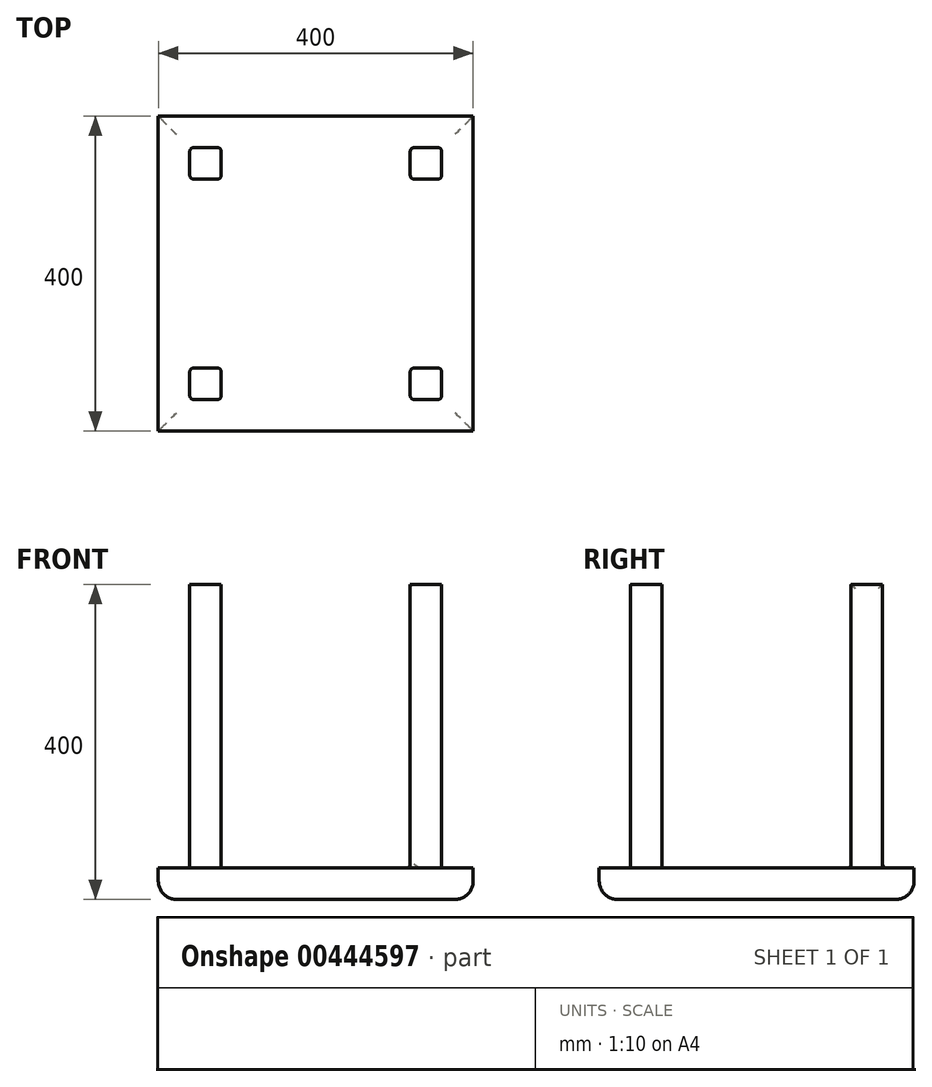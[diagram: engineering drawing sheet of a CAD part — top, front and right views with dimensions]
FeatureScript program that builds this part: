
annotation { "Feature Type Name" : "Feature", "Feature Type Description" : "" }
export const myFeature = defineFeature(function(context is Context, id is Id, definition is map)
    precondition{}
    {
        {
            var Q0;
            Q0=qCreatedBy(makeId("Top.planeOp"),FACE);
            var sketch = newSketch(context, id + "F0", { "sketchPlane" : qUnion([Q0])});
            skLineSegment(sketch, "E0.bottom", {"start": v(-209.5, 229.57) * mm, "end": v(190.5, 229.57) * mm});
            skLineSegment(sketch, "E0.top", {"start": v(-209.5, -170.43) * mm, "end": v(190.5, -170.43) * mm});
            skLineSegment(sketch, "E0.left", {"start": v(-209.5, 229.57) * mm, "end": v(-209.5, -170.43) * mm});
            skLineSegment(sketch, "E0.right", {"start": v(190.5, 229.57) * mm, "end": v(190.5, -170.43) * mm});
            skSolve(sketch);
        }
        {
            var Q0;
            Q0=makeQuery(id+"F0.imprint","IMPRINT",FACE,{"disambiguationData":[TD([[makeQuery(id+"F0.imprint","IMPRINT",EDGE,{"derivedFrom":sQuery(id+"F0.wireOp",EDGE,"E0.bottom")}),-1.0]])]});
            extrude(context, id + "F1", {"entities" : qUnion([Q0]), "depth" : 40 * mm});
        }
        {
            var Q0;
            Q0=makeQuery(id+"F1.opExtrude","CAP_FACE",FACE,{"disambiguationData":[OSD([sQuery(id+"F0.wireOp",EDGE,"E0.bottom"),sQuery(id+"F0.wireOp",EDGE,"E0.top"),sQuery(id+"F0.wireOp",EDGE,"E0.left"),sQuery(id+"F0.wireOp",EDGE,"E0.right")])],"isStart":false});
            var sketch = newSketch(context, id + "F2", { "sketchPlane" : qUnion([Q0])});
            skLineSegment(sketch, "E1.bottom", {"start": v(-169.5, 189.57) * mm, "end": v(-129.5, 189.57) * mm});
            skLineSegment(sketch, "E1.top", {"start": v(-169.5, 149.57) * mm, "end": v(-129.5, 149.57) * mm});
            skLineSegment(sketch, "E1.left", {"start": v(-169.5, 189.57) * mm, "end": v(-169.5, 149.57) * mm});
            skLineSegment(sketch, "E1.right", {"start": v(-129.5, 189.57) * mm, "end": v(-129.5, 149.57) * mm});
            skLineSegment(sketch, "E2.bottom", {"start": v(-169.5, -90.43) * mm, "end": v(-129.5, -90.43) * mm});
            skLineSegment(sketch, "E2.top", {"start": v(-169.5, -130.43) * mm, "end": v(-129.5, -130.43) * mm});
            skLineSegment(sketch, "E2.left", {"start": v(-169.5, -90.43) * mm, "end": v(-169.5, -130.43) * mm});
            skLineSegment(sketch, "E2.right", {"start": v(-129.5, -90.43) * mm, "end": v(-129.5, -130.43) * mm});
            skLineSegment(sketch, "E3.bottom", {"start": v(110.5, -90.43) * mm, "end": v(150.5, -90.43) * mm});
            skLineSegment(sketch, "E3.top", {"start": v(110.5, -130.43) * mm, "end": v(150.5, -130.43) * mm});
            skLineSegment(sketch, "E3.left", {"start": v(110.5, -90.43) * mm, "end": v(110.5, -130.43) * mm});
            skLineSegment(sketch, "E3.right", {"start": v(150.5, -90.43) * mm, "end": v(150.5, -130.43) * mm});
            skLineSegment(sketch, "E4.bottom", {"start": v(110.5, 189.57) * mm, "end": v(150.5, 189.57) * mm});
            skLineSegment(sketch, "E4.top", {"start": v(110.5, 149.57) * mm, "end": v(150.5, 149.57) * mm});
            skLineSegment(sketch, "E4.left", {"start": v(110.5, 189.57) * mm, "end": v(110.5, 149.57) * mm});
            skLineSegment(sketch, "E4.right", {"start": v(150.5, 189.57) * mm, "end": v(150.5, 149.57) * mm});
            skSolve(sketch);
        }
        {
            var Q0;
            Q0=makeQuery(id+"F2.imprint","IMPRINT",FACE,{"disambiguationData":[TD([[makeQuery(id+"F2.imprint","IMPRINT",EDGE,{"derivedFrom":sQuery(id+"F2.wireOp",EDGE,"E3.bottom")}),-1.0]])]});
            var Q1;
            Q1=makeQuery(id+"F2.imprint","IMPRINT",FACE,{"disambiguationData":[TD([[makeQuery(id+"F2.imprint","IMPRINT",EDGE,{"derivedFrom":sQuery(id+"F2.wireOp",EDGE,"E2.bottom")}),-1.0]])]});
            var Q2;
            Q2=makeQuery(id+"F2.imprint","IMPRINT",FACE,{"disambiguationData":[TD([[makeQuery(id+"F2.imprint","IMPRINT",EDGE,{"derivedFrom":sQuery(id+"F2.wireOp",EDGE,"E1.bottom")}),-1.0]])]});
            var Q3;
            Q3=makeQuery(id+"F2.imprint","IMPRINT",FACE,{"disambiguationData":[TD([[makeQuery(id+"F2.imprint","IMPRINT",EDGE,{"derivedFrom":sQuery(id+"F2.wireOp",EDGE,"E4.bottom")}),-1.0]])]});
            extrude(context, id + "F3", {"entities" : qUnion([Q0, Q1, Q2, Q3]), "operationType" : NewBodyOperationType.ADD, "depth" : 360 * mm});
        }
        {
            var Q0;
            Q0=makeQuery(id+"F1.opExtrude","CAP_EDGE",EDGE,{"disambiguationData":[OSD([sQuery(id+"F0.wireOp",EDGE,"E0.left")])],"isStart":true});
            var Q1;
            Q1=makeQuery(id+"F1.opExtrude","CAP_EDGE",EDGE,{"disambiguationData":[OSD([sQuery(id+"F0.wireOp",EDGE,"E0.bottom")])],"isStart":true});
            var Q2;
            Q2=makeQuery(id+"F1.opExtrude","CAP_FACE",FACE,{"disambiguationData":[OSD([sQuery(id+"F0.wireOp",EDGE,"E0.bottom"),sQuery(id+"F0.wireOp",EDGE,"E0.top"),sQuery(id+"F0.wireOp",EDGE,"E0.left"),sQuery(id+"F0.wireOp",EDGE,"E0.right")])],"isStart":true});
            fillet(context, id + "F4", {"entities" : qUnion([Q0, Q1, Q2]), "radius" : 23.1 * mm, "tangentPropagation" : true, "allowEdgeOverflow" : false});
        }
        {
            var Q0;
            Q0=makeQuery(id+"F3.opExtrude","SWEPT_EDGE",EDGE,{"disambiguationData":[OSD([sQuery(id+"F2.wireOp",EDGE,"E1.bottom"),sQuery(id+"F2.wireOp",EDGE,"E1.right")])]});
            var Q1;
            Q1=makeQuery(id+"F3.opExtrude","SWEPT_EDGE",EDGE,{"disambiguationData":[OSD([sQuery(id+"F2.wireOp",EDGE,"E1.top"),sQuery(id+"F2.wireOp",EDGE,"E1.right")])]});
            var Q2;
            Q2=makeQuery(id+"F3.opExtrude","SWEPT_EDGE",EDGE,{"disambiguationData":[OSD([sQuery(id+"F2.wireOp",EDGE,"E2.top"),sQuery(id+"F2.wireOp",EDGE,"E2.left")])]});
            var Q3;
            Q3=makeQuery(id+"F3.opExtrude","SWEPT_EDGE",EDGE,{"disambiguationData":[OSD([sQuery(id+"F2.wireOp",EDGE,"E2.top"),sQuery(id+"F2.wireOp",EDGE,"E2.right")])]});
            var Q4;
            Q4=makeQuery(id+"F3.opExtrude","SWEPT_EDGE",EDGE,{"disambiguationData":[OSD([sQuery(id+"F2.wireOp",EDGE,"E2.bottom"),sQuery(id+"F2.wireOp",EDGE,"E2.right")])]});
            var Q5;
            Q5=makeQuery(id+"F3.opExtrude","SWEPT_EDGE",EDGE,{"disambiguationData":[OSD([sQuery(id+"F2.wireOp",EDGE,"E2.bottom"),sQuery(id+"F2.wireOp",EDGE,"E2.left")])]});
            var Q6;
            Q6=makeQuery(id+"F3.opExtrude","SWEPT_EDGE",EDGE,{"disambiguationData":[OSD([sQuery(id+"F2.wireOp",EDGE,"E1.bottom"),sQuery(id+"F2.wireOp",EDGE,"E1.left")])]});
            var Q7;
            Q7=makeQuery(id+"F3.opExtrude","SWEPT_EDGE",EDGE,{"disambiguationData":[OSD([sQuery(id+"F2.wireOp",EDGE,"E1.top"),sQuery(id+"F2.wireOp",EDGE,"E1.left")])]});
            fillet(context, id + "F5", {"entities" : qUnion([Q0, Q1, Q2, Q3, Q4, Q5, Q6, Q7]), "radius" : 5 * mm, "tangentPropagation" : true, "allowEdgeOverflow" : false});
        }
        {
            var Q0;
            Q0=makeQuery(id+"F3.opExtrude","SWEPT_EDGE",EDGE,{"disambiguationData":[OSD([sQuery(id+"F2.wireOp",EDGE,"E3.top"),sQuery(id+"F2.wireOp",EDGE,"E3.right")])]});
            var Q1;
            Q1=makeQuery(id+"F3.opExtrude","SWEPT_EDGE",EDGE,{"disambiguationData":[OSD([sQuery(id+"F2.wireOp",EDGE,"E3.bottom"),sQuery(id+"F2.wireOp",EDGE,"E3.right")])]});
            var Q2;
            Q2=makeQuery(id+"F3.opExtrude","SWEPT_EDGE",EDGE,{"disambiguationData":[OSD([sQuery(id+"F2.wireOp",EDGE,"E4.top"),sQuery(id+"F2.wireOp",EDGE,"E4.right")])]});
            var Q3;
            Q3=makeQuery(id+"F3.opExtrude","SWEPT_EDGE",EDGE,{"disambiguationData":[OSD([sQuery(id+"F2.wireOp",EDGE,"E4.bottom"),sQuery(id+"F2.wireOp",EDGE,"E4.right")])]});
            var Q4;
            Q4=makeQuery(id+"F3.opExtrude","SWEPT_FACE",FACE,{"disambiguationData":[OSD([sQuery(id+"F2.wireOp",EDGE,"E4.left")])]});
            var Q5;
            Q5=makeQuery(id+"F3.opExtrude","SWEPT_EDGE",EDGE,{"disambiguationData":[OSD([sQuery(id+"F2.wireOp",EDGE,"E4.top"),sQuery(id+"F2.wireOp",EDGE,"E4.left")])]});
            var Q6;
            Q6=makeQuery(id+"F3.opExtrude","SWEPT_EDGE",EDGE,{"disambiguationData":[OSD([sQuery(id+"F2.wireOp",EDGE,"E3.bottom"),sQuery(id+"F2.wireOp",EDGE,"E3.left")])]});
            var Q7;
            Q7=makeQuery(id+"F3.opExtrude","SWEPT_EDGE",EDGE,{"disambiguationData":[OSD([sQuery(id+"F2.wireOp",EDGE,"E3.top"),sQuery(id+"F2.wireOp",EDGE,"E3.left")])]});
            fillet(context, id + "F6", {"entities" : qUnion([Q0, Q1, Q2, Q3, Q4, Q5, Q6, Q7]), "radius" : 5 * mm, "tangentPropagation" : true, "allowEdgeOverflow" : false});
        }
    });
